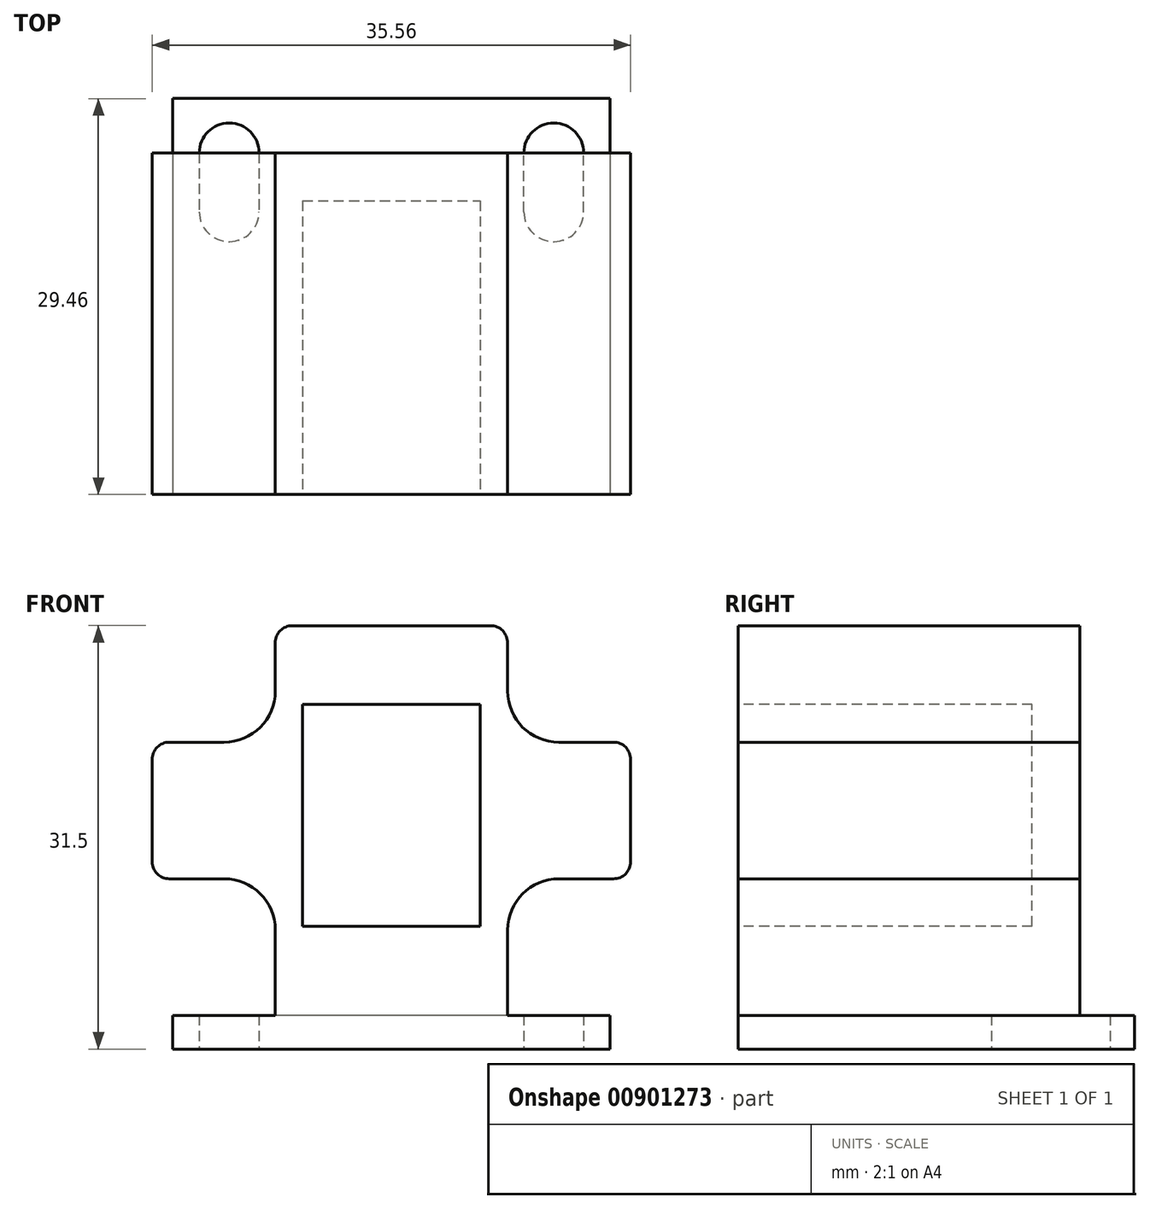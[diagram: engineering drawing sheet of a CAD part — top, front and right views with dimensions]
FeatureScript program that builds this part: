
annotation { "Feature Type Name" : "Feature", "Feature Type Description" : "" }
export const myFeature = defineFeature(function(context is Context, id is Id, definition is map)
    precondition{}
    {
        {
            var Q0;
            Q0=qCreatedBy(makeId("Front.planeOp"),FACE);
            var sketch = newSketch(context, id + "F0", { "sketchPlane" : qUnion([Q0])});
            skLineSegment(sketch, "E0.bottom", {"start": v(-16.26, 0) * mm, "end": v(16.26, 0) * mm});
            skLineSegment(sketch, "E0.top", {"start": v(-16.26, 2.5) * mm, "end": v(16.26, 2.5) * mm});
            skLineSegment(sketch, "E0.left", {"start": v(-16.26, 0) * mm, "end": v(-16.26, 2.5) * mm});
            skLineSegment(sketch, "E0.right", {"start": v(16.26, 0) * mm, "end": v(16.26, 2.5) * mm});
            skLineSegment(sketch, "E1.bottom", {"start": v(-8.64, 2.5) * mm, "end": v(8.64, 2.5) * mm});
            skLineSegment(sketch, "E1.top", {"start": v(-8.64, 12.67) * mm, "end": v(8.64, 12.67) * mm});
            skLineSegment(sketch, "E1.left", {"start": v(-8.64, 2.5) * mm, "end": v(-8.64, 12.67) * mm});
            skLineSegment(sketch, "E1.right", {"start": v(8.64, 2.5) * mm, "end": v(8.64, 12.67) * mm});
            skLineSegment(sketch, "E2.bottom", {"start": v(-17.78, 12.67) * mm, "end": v(17.78, 12.67) * mm});
            skLineSegment(sketch, "E2.top", {"start": v(-17.78, 22.83) * mm, "end": v(17.78, 22.83) * mm});
            skLineSegment(sketch, "E2.left", {"start": v(-17.78, 12.67) * mm, "end": v(-17.78, 22.83) * mm});
            skLineSegment(sketch, "E2.right", {"start": v(17.78, 12.67) * mm, "end": v(17.78, 22.83) * mm});
            skLineSegment(sketch, "E3.bottom", {"start": v(-8.64, 22.83) * mm, "end": v(8.64, 22.83) * mm});
            skLineSegment(sketch, "E3.top", {"start": v(-8.64, 31.5) * mm, "end": v(8.64, 31.5) * mm});
            skLineSegment(sketch, "E3.left", {"start": v(-8.64, 22.83) * mm, "end": v(-8.64, 31.5) * mm});
            skLineSegment(sketch, "E3.right", {"start": v(8.64, 22.83) * mm, "end": v(8.64, 31.5) * mm});
            skSolve(sketch);
        }
        {
            var Q0;
            Q0 = qSketchRegion(id + "F0", true);
            extrude(context, id + "F1", {"entities" : qUnion([Q0]), "oppositeDirection" : true, "depth" : 25.4 * mm, "offsetDistance" : 25.4 * mm});
        }
        {
            var Q0;
            Q0=makeQuery(id+"F1.opExtrude","CAP_FACE",FACE,{"disambiguationData":[OSD([sQuery(id+"F0.wireOp",EDGE,"E0.bottom"),sQuery(id+"F0.wireOp",EDGE,"E0.top"),sQuery(id+"F0.wireOp",EDGE,"E0.left"),sQuery(id+"F0.wireOp",EDGE,"E0.right"),sQuery(id+"F0.wireOp",EDGE,"E1.left"),sQuery(id+"F0.wireOp",EDGE,"E1.right"),sQuery(id+"F0.wireOp",EDGE,"E2.bottom"),sQuery(id+"F0.wireOp",EDGE,"E2.top"),sQuery(id+"F0.wireOp",EDGE,"E2.left"),sQuery(id+"F0.wireOp",EDGE,"E2.right"),sQuery(id+"F0.wireOp",EDGE,"E3.top"),sQuery(id+"F0.wireOp",EDGE,"E3.left"),sQuery(id+"F0.wireOp",EDGE,"E3.right")])],"isStart":false});
            var sketch = newSketch(context, id + "F2", { "sketchPlane" : qUnion([Q0])});
            skLineSegment(sketch, "E4.bottom", {"start": v(-16.26, 0) * mm, "end": v(16.26, 0) * mm});
            skLineSegment(sketch, "E4.top", {"start": v(-16.26, 2.5) * mm, "end": v(16.26, 2.5) * mm});
            skLineSegment(sketch, "E4.left", {"start": v(-16.26, 0) * mm, "end": v(-16.26, 2.5) * mm});
            skLineSegment(sketch, "E4.right", {"start": v(16.26, 0) * mm, "end": v(16.26, 2.5) * mm});
            skSolve(sketch);
        }
        {
            var Q0;
            Q0 = qSketchRegion(id + "F2", true);
            extrude(context, id + "F3", {"entities" : qUnion([Q0]), "operationType" : NewBodyOperationType.ADD, "depth" : 4.06 * mm, "offsetDistance" : 25.4 * mm});
        }
        {
            var Q0;
            Q0=makeQuery(id+"F1.opExtrude","SWEPT_EDGE",EDGE,{"disambiguationData":[OSD([sQuery(id+"F0.wireOp",EDGE,"E2.top"),sQuery(id+"F0.wireOp",EDGE,"E3.bottom"),sQuery(id+"F0.wireOp",EDGE,"E3.left")])]});
            var Q1;
            Q1=makeQuery(id+"F1.opExtrude","SWEPT_EDGE",EDGE,{"disambiguationData":[OSD([sQuery(id+"F0.wireOp",EDGE,"E1.left"),sQuery(id+"F0.wireOp",EDGE,"E2.bottom")])]});
            var Q2;
            Q2=makeQuery(id+"F1.opExtrude","SWEPT_EDGE",EDGE,{"disambiguationData":[OSD([sQuery(id+"F0.wireOp",EDGE,"E1.right"),sQuery(id+"F0.wireOp",EDGE,"E2.bottom")])]});
            var Q3;
            Q3=makeQuery(id+"F1.opExtrude","SWEPT_EDGE",EDGE,{"disambiguationData":[OSD([sQuery(id+"F0.wireOp",EDGE,"E2.top"),sQuery(id+"F0.wireOp",EDGE,"E3.bottom"),sQuery(id+"F0.wireOp",EDGE,"E3.right")])]});
            fillet(context, id + "F4", {"entities" : qUnion([Q0, Q1, Q2, Q3]), "radius" : 3.8 * mm, "tangentPropagation" : true, "allowEdgeOverflow" : false});
        }
        {
            var Q0;
            Q0=makeQuery(id+"F1.opExtrude","SWEPT_EDGE",EDGE,{"disambiguationData":[OSD([sQuery(id+"F0.wireOp",EDGE,"E3.top"),sQuery(id+"F0.wireOp",EDGE,"E3.left")])]});
            var Q1;
            Q1=makeQuery(id+"F1.opExtrude","SWEPT_EDGE",EDGE,{"disambiguationData":[OSD([sQuery(id+"F0.wireOp",EDGE,"E3.top"),sQuery(id+"F0.wireOp",EDGE,"E3.right")])]});
            var Q2;
            Q2=makeQuery(id+"F1.opExtrude","SWEPT_EDGE",EDGE,{"disambiguationData":[OSD([sQuery(id+"F0.wireOp",EDGE,"E2.top"),sQuery(id+"F0.wireOp",EDGE,"E2.right")])]});
            var Q3;
            Q3=makeQuery(id+"F1.opExtrude","SWEPT_EDGE",EDGE,{"disambiguationData":[OSD([sQuery(id+"F0.wireOp",EDGE,"E2.bottom"),sQuery(id+"F0.wireOp",EDGE,"E2.right")])]});
            var Q4;
            Q4=makeQuery(id+"F1.opExtrude","SWEPT_EDGE",EDGE,{"disambiguationData":[OSD([sQuery(id+"F0.wireOp",EDGE,"E2.bottom"),sQuery(id+"F0.wireOp",EDGE,"E2.left")])]});
            var Q5;
            Q5=makeQuery(id+"F1.opExtrude","SWEPT_EDGE",EDGE,{"disambiguationData":[OSD([sQuery(id+"F0.wireOp",EDGE,"E2.top"),sQuery(id+"F0.wireOp",EDGE,"E2.left")])]});
            fillet(context, id + "F5", {"entities" : qUnion([Q0, Q1, Q2, Q3, Q4, Q5]), "radius" : 1.27 * mm, "tangentPropagation" : true, "allowEdgeOverflow" : false});
        }
        {
            var Q0;
            Q0=makeQuery(id+"F1.opExtrude","CAP_FACE",FACE,{"disambiguationData":[OSD([sQuery(id+"F0.wireOp",EDGE,"E0.bottom"),sQuery(id+"F0.wireOp",EDGE,"E0.top"),sQuery(id+"F0.wireOp",EDGE,"E0.left"),sQuery(id+"F0.wireOp",EDGE,"E0.right"),sQuery(id+"F0.wireOp",EDGE,"E1.left"),sQuery(id+"F0.wireOp",EDGE,"E1.right"),sQuery(id+"F0.wireOp",EDGE,"E2.bottom"),sQuery(id+"F0.wireOp",EDGE,"E2.top"),sQuery(id+"F0.wireOp",EDGE,"E2.left"),sQuery(id+"F0.wireOp",EDGE,"E2.right"),sQuery(id+"F0.wireOp",EDGE,"E3.top"),sQuery(id+"F0.wireOp",EDGE,"E3.left"),sQuery(id+"F0.wireOp",EDGE,"E3.right")])],"isStart":true});
            var sketch = newSketch(context, id + "F6", { "sketchPlane" : qUnion([Q0])});
            skLineSegment(sketch, "E5.bottom", {"start": v(-6.6, 9.14) * mm, "end": v(6.6, 9.14) * mm});
            skLineSegment(sketch, "E5.top", {"start": v(-6.6, 25.65) * mm, "end": v(6.6, 25.65) * mm});
            skLineSegment(sketch, "E5.left", {"start": v(-6.6, 9.14) * mm, "end": v(-6.6, 25.65) * mm});
            skLineSegment(sketch, "E5.right", {"start": v(6.6, 9.14) * mm, "end": v(6.6, 25.65) * mm});
            skSolve(sketch);
        }
        {
            var Q0;
            Q0 = qSketchRegion(id + "F6", true);
            extrude(context, id + "F7", {"entities" : qUnion([Q0]), "operationType" : NewBodyOperationType.REMOVE, "oppositeDirection" : true, "depth" : 21.84 * mm, "offsetDistance" : 25.4 * mm});
        }
        {
            var Q0;
            Q0=makeQuery(id+"F3.boolean.opBoolean","MERGE",FACE,{"derivedFrom":[makeQuery(id+"F1.opExtrude","SWEPT_FACE",FACE,{"disambiguationData":[OSD([sQuery(id+"F0.wireOp",EDGE,"E0.bottom")])]}),makeQuery(id+"F3.opExtrude","SWEPT_FACE",FACE,{"disambiguationData":[OSD([sQuery(id+"F2.wireOp",EDGE,"E4.bottom")])]})]});
            var sketch = newSketch(context, id + "F8", { "sketchPlane" : qUnion([Q0])});
            skLineSegment(sketch, "E6.bottom", {"start": v(-12.08, -27.64) * mm, "end": v(-12.05, -27.64) * mm});
            skLineSegment(sketch, "E6.top", {"start": v(-12.08, -18.82) * mm, "end": v(-12.05, -18.82) * mm});
            skLineSegment(sketch, "E6.left", {"start": v(-14.29, -25.43) * mm, "end": v(-14.29, -21.03) * mm});
            skLineSegment(sketch, "E6.right", {"start": v(-9.84, -25.43) * mm, "end": v(-9.84, -21.03) * mm});
            skLineSegment(sketch, "E7.bottom", {"start": v(12.05, -18.82) * mm, "end": v(12.08, -18.82) * mm});
            skLineSegment(sketch, "E7.top", {"start": v(12.05, -27.64) * mm, "end": v(12.08, -27.64) * mm});
            skLineSegment(sketch, "E7.left", {"start": v(9.84, -21.03) * mm, "end": v(9.84, -25.43) * mm});
            skLineSegment(sketch, "E7.right", {"start": v(14.29, -21.03) * mm, "end": v(14.29, -25.43) * mm});
            skPoint(sketch, "E8.visualSharp", {"position": v(-14.29, -27.64) * mm});
            skArc(sketch, "E8.filletArc", {"start": v(-14.29, -25.43) * mm, "mid": v(-13.64, -26.99) * mm, "end": v(-12.08, -27.64) * mm});
            skPoint(sketch, "E9.visualSharp", {"position": v(-9.84, -27.64) * mm});
            skArc(sketch, "E9.filletArc", {"start": v(-12.05, -27.64) * mm, "mid": v(-10.49, -26.99) * mm, "end": v(-9.84, -25.43) * mm});
            skPoint(sketch, "E10.visualSharp", {"position": v(-9.84, -18.82) * mm});
            skArc(sketch, "E10.filletArc", {"start": v(-9.84, -21.03) * mm, "mid": v(-10.49, -19.47) * mm, "end": v(-12.05, -18.82) * mm});
            skPoint(sketch, "E11.visualSharp", {"position": v(-14.29, -18.82) * mm});
            skArc(sketch, "E11.filletArc", {"start": v(-12.08, -18.82) * mm, "mid": v(-13.64, -19.47) * mm, "end": v(-14.29, -21.03) * mm});
            skPoint(sketch, "E12.visualSharp", {"position": v(9.84, -18.82) * mm});
            skArc(sketch, "E12.filletArc", {"start": v(12.05, -18.82) * mm, "mid": v(10.49, -19.47) * mm, "end": v(9.84, -21.03) * mm});
            skPoint(sketch, "E13.visualSharp", {"position": v(14.29, -18.82) * mm});
            skArc(sketch, "E13.filletArc", {"start": v(14.29, -21.03) * mm, "mid": v(13.64, -19.47) * mm, "end": v(12.08, -18.82) * mm});
            skPoint(sketch, "E14.visualSharp", {"position": v(14.29, -27.64) * mm});
            skArc(sketch, "E14.filletArc", {"start": v(12.08, -27.64) * mm, "mid": v(13.64, -26.99) * mm, "end": v(14.29, -25.43) * mm});
            skPoint(sketch, "E15.visualSharp", {"position": v(9.84, -27.64) * mm});
            skArc(sketch, "E15.filletArc", {"start": v(9.84, -25.43) * mm, "mid": v(10.49, -26.99) * mm, "end": v(12.05, -27.64) * mm});
            skSolve(sketch);
        }
        {
            var Q0;
            Q0 = qSketchRegion(id + "F8", true);
            extrude(context, id + "F9", {"entities" : qUnion([Q0]), "operationType" : NewBodyOperationType.REMOVE, "oppositeDirection" : true, "depth" : 5.08 * mm, "offsetDistance" : 25.4 * mm});
        }
    });
